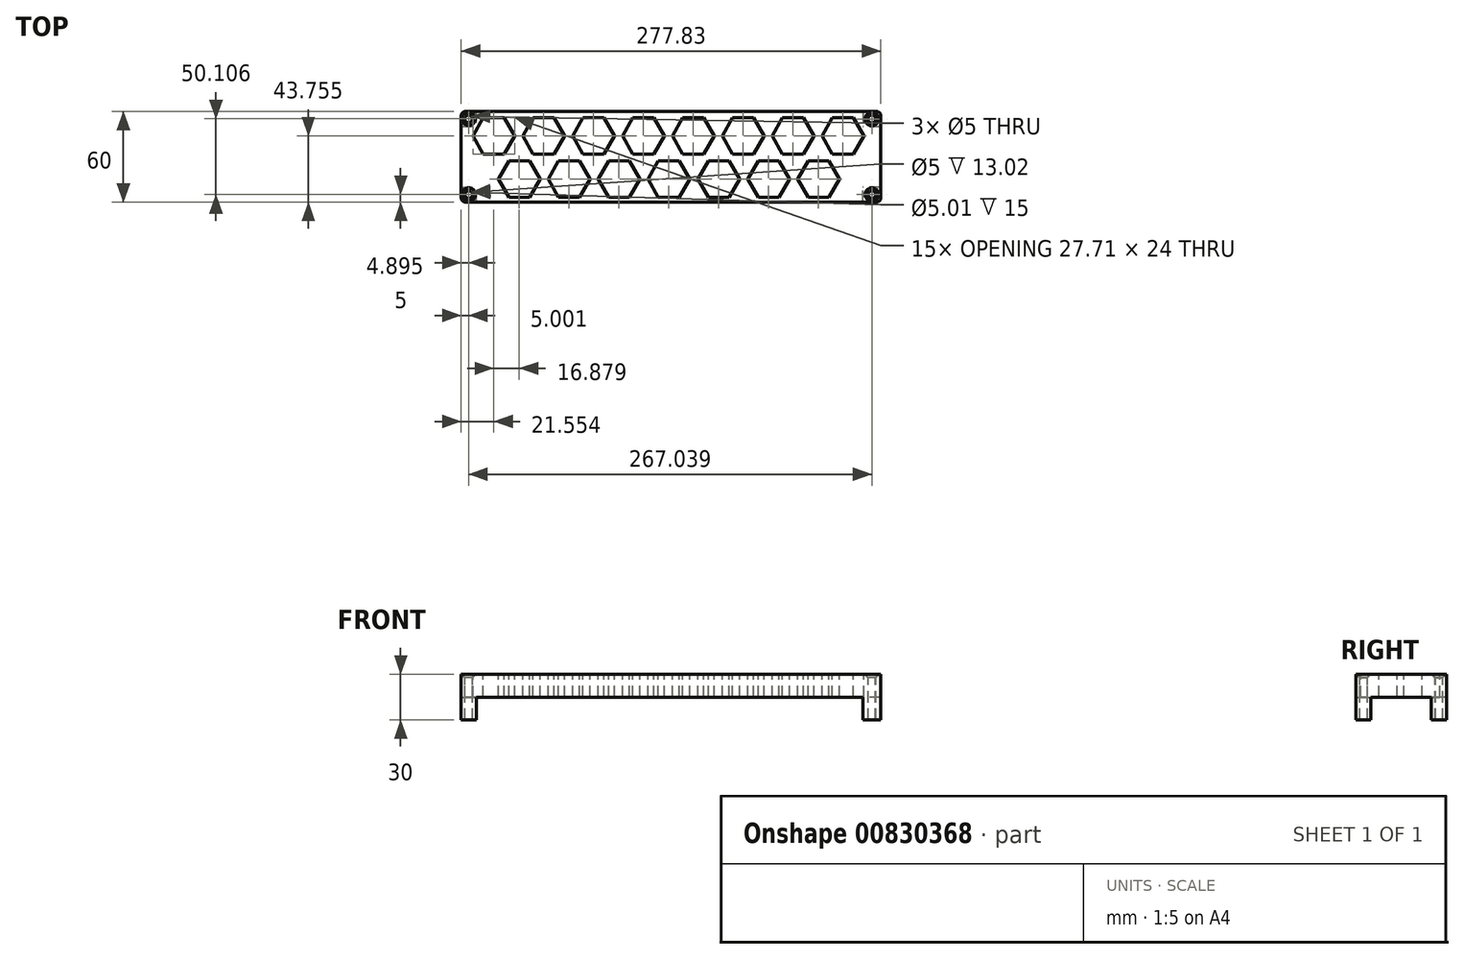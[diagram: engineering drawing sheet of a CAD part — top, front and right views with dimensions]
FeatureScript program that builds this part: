
annotation { "Feature Type Name" : "Feature", "Feature Type Description" : "" }
export const myFeature = defineFeature(function(context is Context, id is Id, definition is map)
    precondition{}
    {
        {
            var Q0;
            Q0=qCreatedBy(makeId("Top.planeOp"),FACE);
            var sketch = newSketch(context, id + "F0", { "sketchPlane" : qUnion([Q0])});
            skLineSegment(sketch, "E0.bottom", {"start": v(-54.94, 35.9) * mm, "end": v(215.06, 35.9) * mm});
            skLineSegment(sketch, "E0.top", {"start": v(-54.94, -24.1) * mm, "end": v(215.06, -24.1) * mm});
            skLineSegment(sketch, "E0.left", {"start": v(-54.94, 35.9) * mm, "end": v(-54.94, -24.1) * mm});
            skLineSegment(sketch, "E1.bottom", {"start": v(215.06, -24.1) * mm, "end": v(222.9, -24.1) * mm});
            skLineSegment(sketch, "E1.right", {"start": v(222.9, -24.1) * mm, "end": v(222.9, 35.9) * mm});
            skLineSegment(sketch, "E2", {"start": v(215.06, 35.9) * mm, "end": v(222.9, 35.9) * mm});
            skSolve(sketch);
        }
        {
            var Q0;
            Q0=makeQuery(id+"F0.imprint","IMPRINT",FACE,{"disambiguationData":[TD([[makeQuery(id+"F0.imprint","IMPRINT",EDGE,{"derivedFrom":sQuery(id+"F0.wireOp",EDGE,"E0.bottom")}),-1.0]])]});
            extrude(context, id + "F1", {"entities" : qUnion([Q0]), "depth" : 15 * mm, "offsetDistance" : 25.4 * mm});
        }
        {
            var Q0;
            Q0=makeQuery(id+"F1.opExtrude","CAP_FACE",FACE,{"disambiguationData":[OSD([sQuery(id+"F0.wireOp",EDGE,"E0.bottom"),sQuery(id+"F0.wireOp",EDGE,"E0.top"),sQuery(id+"F0.wireOp",EDGE,"E0.left"),sQuery(id+"F0.wireOp",EDGE,"E0.right")])],"isStart":false});
            var sketch = newSketch(context, id + "F2", { "sketchPlane" : qUnion([Q0])});
            skCircle(sketch, "E3.cCircle", {"center": v(-33.39, 19.66) * mm, "radius": 12 * mm, "construction": true});
            skLineSegment(sketch, "E3.0", {"start": v(-26.46, 7.66) * mm, "end": v(-40.31, 7.66) * mm});
            skLineSegment(sketch, "E3.1", {"start": v(-40.31, 7.66) * mm, "end": v(-47.24, 19.66) * mm});
            skLineSegment(sketch, "E3.2", {"start": v(-47.24, 19.66) * mm, "end": v(-40.31, 31.66) * mm});
            skLineSegment(sketch, "E3.3", {"start": v(-40.31, 31.66) * mm, "end": v(-26.46, 31.66) * mm});
            skLineSegment(sketch, "E3.4", {"start": v(-26.46, 31.66) * mm, "end": v(-19.53, 19.66) * mm});
            skLineSegment(sketch, "E3.5", {"start": v(-19.53, 19.66) * mm, "end": v(-26.46, 7.66) * mm});
            skPoint(sketch, "E3.0.midPoint", {"position": v(-33.39, 7.66) * mm});
            skLineSegment(sketch, "E4.1.0.0", {"start": v(6.56, 31.66) * mm, "end": v(13.5, 19.66) * mm});
            skLineSegment(sketch, "E4.1.0.1", {"start": v(-7.3, 31.66) * mm, "end": v(6.56, 31.66) * mm});
            skCircle(sketch, "E4.1.0.2", {"center": v(-0.37, 19.66) * mm, "radius": 12 * mm, "construction": true});
            skLineSegment(sketch, "E4.1.0.3", {"start": v(-14.22, 19.66) * mm, "end": v(-7.3, 31.66) * mm});
            skLineSegment(sketch, "E4.1.0.4", {"start": v(-7.3, 7.66) * mm, "end": v(-14.22, 19.66) * mm});
            skLineSegment(sketch, "E4.1.0.5", {"start": v(6.56, 7.66) * mm, "end": v(-7.3, 7.66) * mm});
            skLineSegment(sketch, "E4.1.0.6", {"start": v(13.5, 19.66) * mm, "end": v(6.56, 7.66) * mm});
            skLineSegment(sketch, "E4.2.0.0", {"start": v(39.58, 31.66) * mm, "end": v(46.51, 19.66) * mm});
            skLineSegment(sketch, "E4.2.0.1", {"start": v(25.73, 31.66) * mm, "end": v(39.58, 31.66) * mm});
            skCircle(sketch, "E4.2.0.2", {"center": v(32.65, 19.66) * mm, "radius": 12 * mm, "construction": true});
            skLineSegment(sketch, "E4.2.0.3", {"start": v(18.8, 19.66) * mm, "end": v(25.73, 31.66) * mm});
            skLineSegment(sketch, "E4.2.0.4", {"start": v(25.73, 7.66) * mm, "end": v(18.8, 19.66) * mm});
            skLineSegment(sketch, "E4.2.0.5", {"start": v(39.58, 7.66) * mm, "end": v(25.73, 7.66) * mm});
            skLineSegment(sketch, "E4.2.0.6", {"start": v(46.51, 19.66) * mm, "end": v(39.58, 7.66) * mm});
            skLineSegment(sketch, "E4.3.0.0", {"start": v(72.6, 31.66) * mm, "end": v(79.53, 19.66) * mm});
            skLineSegment(sketch, "E4.3.0.1", {"start": v(58.75, 31.66) * mm, "end": v(72.6, 31.66) * mm});
            skCircle(sketch, "E4.3.0.2", {"center": v(65.67, 19.66) * mm, "radius": 12 * mm, "construction": true});
            skLineSegment(sketch, "E4.3.0.3", {"start": v(51.82, 19.66) * mm, "end": v(58.75, 31.66) * mm});
            skLineSegment(sketch, "E4.3.0.4", {"start": v(58.75, 7.66) * mm, "end": v(51.82, 19.66) * mm});
            skLineSegment(sketch, "E4.3.0.5", {"start": v(72.6, 7.66) * mm, "end": v(58.75, 7.66) * mm});
            skLineSegment(sketch, "E4.3.0.6", {"start": v(79.53, 19.66) * mm, "end": v(72.6, 7.66) * mm});
            skLineSegment(sketch, "E4.4.0.0", {"start": v(105.62, 31.66) * mm, "end": v(112.55, 19.66) * mm});
            skLineSegment(sketch, "E4.4.0.1", {"start": v(91.77, 31.66) * mm, "end": v(105.62, 31.66) * mm});
            skCircle(sketch, "E4.4.0.2", {"center": v(98.7, 19.66) * mm, "radius": 12 * mm, "construction": true});
            skLineSegment(sketch, "E4.4.0.3", {"start": v(84.84, 19.66) * mm, "end": v(91.77, 31.66) * mm});
            skLineSegment(sketch, "E4.4.0.4", {"start": v(91.77, 7.66) * mm, "end": v(84.84, 19.66) * mm});
            skLineSegment(sketch, "E4.4.0.5", {"start": v(105.62, 7.66) * mm, "end": v(91.77, 7.66) * mm});
            skLineSegment(sketch, "E4.4.0.6", {"start": v(112.55, 19.66) * mm, "end": v(105.62, 7.66) * mm});
            skLineSegment(sketch, "E4.5.0.0", {"start": v(138.64, 31.66) * mm, "end": v(145.57, 19.66) * mm});
            skLineSegment(sketch, "E4.5.0.1", {"start": v(124.79, 31.66) * mm, "end": v(138.64, 31.66) * mm});
            skCircle(sketch, "E4.5.0.2", {"center": v(131.71, 19.66) * mm, "radius": 12 * mm, "construction": true});
            skLineSegment(sketch, "E4.5.0.3", {"start": v(117.86, 19.66) * mm, "end": v(124.79, 31.66) * mm});
            skLineSegment(sketch, "E4.5.0.4", {"start": v(124.79, 7.66) * mm, "end": v(117.86, 19.66) * mm});
            skLineSegment(sketch, "E4.5.0.5", {"start": v(138.64, 7.66) * mm, "end": v(124.79, 7.66) * mm});
            skLineSegment(sketch, "E4.5.0.6", {"start": v(145.57, 19.66) * mm, "end": v(138.64, 7.66) * mm});
            skLineSegment(sketch, "E4.6.0.0", {"start": v(171.66, 31.66) * mm, "end": v(178.6, 19.66) * mm});
            skLineSegment(sketch, "E4.6.0.1", {"start": v(157.8, 31.66) * mm, "end": v(171.66, 31.66) * mm});
            skCircle(sketch, "E4.6.0.2", {"center": v(164.73, 19.66) * mm, "radius": 12 * mm, "construction": true});
            skLineSegment(sketch, "E4.6.0.3", {"start": v(150.88, 19.66) * mm, "end": v(157.8, 31.66) * mm});
            skLineSegment(sketch, "E4.6.0.4", {"start": v(157.8, 7.66) * mm, "end": v(150.88, 19.66) * mm});
            skLineSegment(sketch, "E4.6.0.5", {"start": v(171.66, 7.66) * mm, "end": v(157.8, 7.66) * mm});
            skLineSegment(sketch, "E4.6.0.6", {"start": v(178.6, 19.66) * mm, "end": v(171.66, 7.66) * mm});
            skLineSegment(sketch, "E4.7.0.0", {"start": v(204.68, 31.66) * mm, "end": v(211.61, 19.66) * mm});
            skLineSegment(sketch, "E4.7.0.1", {"start": v(190.83, 31.66) * mm, "end": v(204.68, 31.66) * mm});
            skCircle(sketch, "E4.7.0.2", {"center": v(197.75, 19.66) * mm, "radius": 12 * mm, "construction": true});
            skLineSegment(sketch, "E4.7.0.3", {"start": v(183.9, 19.66) * mm, "end": v(190.83, 31.66) * mm});
            skLineSegment(sketch, "E4.7.0.4", {"start": v(190.83, 7.66) * mm, "end": v(183.9, 19.66) * mm});
            skLineSegment(sketch, "E4.7.0.5", {"start": v(204.68, 7.66) * mm, "end": v(190.83, 7.66) * mm});
            skLineSegment(sketch, "E4.7.0.6", {"start": v(211.61, 19.66) * mm, "end": v(204.68, 7.66) * mm});
            skLineSegment(sketch, "E4.direction1", {"start": v(-19.53, 19.66) * mm, "end": v(13.5, 19.66) * mm, "construction": true});
            skSolve(sketch);
        }
        {
            var Q0;
            Q0=makeQuery(id+"F2.imprint","IMPRINT",FACE,{"disambiguationData":[TD([[makeQuery(id+"F2.imprint","IMPRINT",EDGE,{"derivedFrom":sQuery(id+"F2.wireOp",EDGE,"E3.0")}),1.0]])]});
            var sketch = newSketch(context, id + "F3", { "sketchPlane" : qUnion([Q0])});
            skCircle(sketch, "E5.cCircle", {"center": v(-16.5, -8.82) * mm, "radius": 12 * mm, "construction": true});
            skLineSegment(sketch, "E5.0", {"start": v(-9.58, -20.82) * mm, "end": v(-23.44, -20.82) * mm});
            skLineSegment(sketch, "E5.1", {"start": v(-23.44, -20.82) * mm, "end": v(-30.36, -8.82) * mm});
            skLineSegment(sketch, "E5.2", {"start": v(-30.36, -8.82) * mm, "end": v(-23.44, 3.18) * mm});
            skLineSegment(sketch, "E5.3", {"start": v(-23.44, 3.18) * mm, "end": v(-9.58, 3.18) * mm});
            skLineSegment(sketch, "E5.4", {"start": v(-9.58, 3.18) * mm, "end": v(-2.65, -8.82) * mm});
            skLineSegment(sketch, "E5.5", {"start": v(-2.65, -8.82) * mm, "end": v(-9.58, -20.82) * mm});
            skPoint(sketch, "E5.0.midPoint", {"position": v(-16.5, -20.82) * mm});
            skLineSegment(sketch, "E6.1.0.0", {"start": v(9.58, 3.18) * mm, "end": v(23.44, 3.18) * mm});
            skLineSegment(sketch, "E6.1.0.1", {"start": v(23.44, 3.18) * mm, "end": v(30.37, -8.82) * mm});
            skLineSegment(sketch, "E6.1.0.2", {"start": v(2.66, -8.82) * mm, "end": v(9.58, 3.18) * mm});
            skLineSegment(sketch, "E6.1.0.3", {"start": v(9.58, -20.82) * mm, "end": v(2.66, -8.82) * mm});
            skLineSegment(sketch, "E6.1.0.4", {"start": v(23.44, -20.82) * mm, "end": v(9.58, -20.82) * mm});
            skLineSegment(sketch, "E6.1.0.5", {"start": v(30.37, -8.82) * mm, "end": v(23.44, -20.82) * mm});
            skLineSegment(sketch, "E6.2.0.0", {"start": v(42.6, 3.18) * mm, "end": v(56.46, 3.18) * mm});
            skLineSegment(sketch, "E6.2.0.1", {"start": v(56.46, 3.18) * mm, "end": v(63.39, -8.82) * mm});
            skLineSegment(sketch, "E6.2.0.2", {"start": v(35.68, -8.82) * mm, "end": v(42.6, 3.18) * mm});
            skLineSegment(sketch, "E6.2.0.3", {"start": v(42.6, -20.82) * mm, "end": v(35.68, -8.82) * mm});
            skLineSegment(sketch, "E6.2.0.4", {"start": v(56.46, -20.82) * mm, "end": v(42.6, -20.82) * mm});
            skLineSegment(sketch, "E6.2.0.5", {"start": v(63.39, -8.82) * mm, "end": v(56.46, -20.82) * mm});
            skLineSegment(sketch, "E6.3.0.0", {"start": v(75.62, 3.18) * mm, "end": v(89.48, 3.18) * mm});
            skLineSegment(sketch, "E6.3.0.1", {"start": v(89.48, 3.18) * mm, "end": v(96.4, -8.82) * mm});
            skLineSegment(sketch, "E6.3.0.2", {"start": v(68.7, -8.82) * mm, "end": v(75.62, 3.18) * mm});
            skLineSegment(sketch, "E6.3.0.3", {"start": v(75.62, -20.82) * mm, "end": v(68.7, -8.82) * mm});
            skLineSegment(sketch, "E6.3.0.4", {"start": v(89.48, -20.82) * mm, "end": v(75.62, -20.82) * mm});
            skLineSegment(sketch, "E6.3.0.5", {"start": v(96.4, -8.82) * mm, "end": v(89.48, -20.82) * mm});
            skLineSegment(sketch, "E6.4.0.0", {"start": v(108.64, 3.18) * mm, "end": v(122.5, 3.18) * mm});
            skLineSegment(sketch, "E6.4.0.1", {"start": v(122.5, 3.18) * mm, "end": v(129.43, -8.82) * mm});
            skLineSegment(sketch, "E6.4.0.2", {"start": v(101.72, -8.82) * mm, "end": v(108.64, 3.18) * mm});
            skLineSegment(sketch, "E6.4.0.3", {"start": v(108.64, -20.82) * mm, "end": v(101.72, -8.82) * mm});
            skLineSegment(sketch, "E6.4.0.4", {"start": v(122.5, -20.82) * mm, "end": v(108.64, -20.82) * mm});
            skLineSegment(sketch, "E6.4.0.5", {"start": v(129.43, -8.82) * mm, "end": v(122.5, -20.82) * mm});
            skLineSegment(sketch, "E6.5.0.0", {"start": v(141.66, 3.18) * mm, "end": v(155.52, 3.18) * mm});
            skLineSegment(sketch, "E6.5.0.1", {"start": v(155.52, 3.18) * mm, "end": v(162.45, -8.82) * mm});
            skLineSegment(sketch, "E6.5.0.2", {"start": v(134.74, -8.82) * mm, "end": v(141.66, 3.18) * mm});
            skLineSegment(sketch, "E6.5.0.3", {"start": v(141.66, -20.82) * mm, "end": v(134.74, -8.82) * mm});
            skLineSegment(sketch, "E6.5.0.4", {"start": v(155.52, -20.82) * mm, "end": v(141.66, -20.82) * mm});
            skLineSegment(sketch, "E6.5.0.5", {"start": v(162.45, -8.82) * mm, "end": v(155.52, -20.82) * mm});
            skLineSegment(sketch, "E6.6.0.0", {"start": v(174.68, 3.18) * mm, "end": v(188.54, 3.18) * mm});
            skLineSegment(sketch, "E6.6.0.1", {"start": v(188.54, 3.18) * mm, "end": v(195.47, -8.82) * mm});
            skLineSegment(sketch, "E6.6.0.2", {"start": v(167.76, -8.82) * mm, "end": v(174.68, 3.18) * mm});
            skLineSegment(sketch, "E6.6.0.3", {"start": v(174.68, -20.82) * mm, "end": v(167.76, -8.82) * mm});
            skLineSegment(sketch, "E6.6.0.4", {"start": v(188.54, -20.82) * mm, "end": v(174.68, -20.82) * mm});
            skLineSegment(sketch, "E6.6.0.5", {"start": v(195.47, -8.82) * mm, "end": v(188.54, -20.82) * mm});
            skLineSegment(sketch, "E6.direction1", {"start": v(-23.44, 3.18) * mm, "end": v(9.58, 3.18) * mm, "construction": true});
            skSolve(sketch);
        }
        {
            var Q0;
            Q0=makeQuery(id+"F2.imprint","IMPRINT",FACE,{"disambiguationData":[TD([[makeQuery(id+"F2.imprint","IMPRINT",EDGE,{"derivedFrom":sQuery(id+"F2.wireOp",EDGE,"E3.0")}),-1.0]])]});
            var Q1;
            Q1=makeQuery(id+"F3.imprint","IMPRINT",FACE,{"disambiguationData":[TD([[makeQuery(id+"F3.imprint","IMPRINT",EDGE,{"derivedFrom":sQuery(id+"F3.wireOp",EDGE,"E5.0")}),-1.0]])]});
            var Q2;
            Q2=makeQuery(id+"F2.imprint","IMPRINT",FACE,{"disambiguationData":[TD([[makeQuery(id+"F2.imprint","IMPRINT",EDGE,{"derivedFrom":sQuery(id+"F2.wireOp",EDGE,"E4.1.0.0")}),-1.0]])]});
            var Q3;
            Q3=makeQuery(id+"F2.imprint","IMPRINT",FACE,{"disambiguationData":[TD([[makeQuery(id+"F2.imprint","IMPRINT",EDGE,{"derivedFrom":sQuery(id+"F2.wireOp",EDGE,"E4.2.0.0")}),-1.0]])]});
            var Q4;
            Q4=makeQuery(id+"F2.imprint","IMPRINT",FACE,{"disambiguationData":[TD([[makeQuery(id+"F2.imprint","IMPRINT",EDGE,{"derivedFrom":sQuery(id+"F2.wireOp",EDGE,"E4.3.0.0")}),-1.0]])]});
            var Q5;
            Q5=makeQuery(id+"F2.imprint","IMPRINT",FACE,{"disambiguationData":[TD([[makeQuery(id+"F2.imprint","IMPRINT",EDGE,{"derivedFrom":sQuery(id+"F2.wireOp",EDGE,"E4.4.0.0")}),-1.0]])]});
            var Q6;
            Q6=makeQuery(id+"F2.imprint","IMPRINT",FACE,{"disambiguationData":[TD([[makeQuery(id+"F2.imprint","IMPRINT",EDGE,{"derivedFrom":sQuery(id+"F2.wireOp",EDGE,"E4.5.0.0")}),-1.0]])]});
            var Q7;
            Q7=makeQuery(id+"F2.imprint","IMPRINT",FACE,{"disambiguationData":[TD([[makeQuery(id+"F2.imprint","IMPRINT",EDGE,{"derivedFrom":sQuery(id+"F2.wireOp",EDGE,"E4.6.0.0")}),-1.0]])]});
            var Q8;
            Q8=makeQuery(id+"F2.imprint","IMPRINT",FACE,{"disambiguationData":[TD([[makeQuery(id+"F2.imprint","IMPRINT",EDGE,{"derivedFrom":sQuery(id+"F2.wireOp",EDGE,"E4.7.0.0")}),-1.0]])]});
            var Q9;
            Q9=makeQuery(id+"F3.imprint","IMPRINT",FACE,{"disambiguationData":[TD([[makeQuery(id+"F3.imprint","IMPRINT",EDGE,{"derivedFrom":sQuery(id+"F3.wireOp",EDGE,"E6.1.0.0")}),-1.0]])]});
            extrude(context, id + "F4", {"entities" : qUnion([Q0, Q1, Q2, Q3, Q4, Q5, Q6, Q7, Q8, Q9]), "operationType" : NewBodyOperationType.REMOVE, "oppositeDirection" : true, "depth" : 61.47 * mm, "offsetDistance" : 25.4 * mm});
        }
        {
            var Q0;
            Q0=makeQuery(id+"F3.imprint","IMPRINT",FACE,{"disambiguationData":[TD([[makeQuery(id+"F3.imprint","IMPRINT",EDGE,{"derivedFrom":sQuery(id+"F3.wireOp",EDGE,"E6.2.0.0")}),-1.0]])]});
            var Q1;
            Q1=makeQuery(id+"F3.imprint","IMPRINT",FACE,{"disambiguationData":[TD([[makeQuery(id+"F3.imprint","IMPRINT",EDGE,{"derivedFrom":sQuery(id+"F3.wireOp",EDGE,"E6.3.0.0")}),-1.0]])]});
            var Q2;
            Q2=makeQuery(id+"F3.imprint","IMPRINT",FACE,{"disambiguationData":[TD([[makeQuery(id+"F3.imprint","IMPRINT",EDGE,{"derivedFrom":sQuery(id+"F3.wireOp",EDGE,"E6.4.0.0")}),-1.0]])]});
            var Q3;
            Q3=makeQuery(id+"F3.imprint","IMPRINT",FACE,{"disambiguationData":[TD([[makeQuery(id+"F3.imprint","IMPRINT",EDGE,{"derivedFrom":sQuery(id+"F3.wireOp",EDGE,"E6.5.0.0")}),-1.0]])]});
            var Q4;
            Q4=makeQuery(id+"F3.imprint","IMPRINT",FACE,{"disambiguationData":[TD([[makeQuery(id+"F3.imprint","IMPRINT",EDGE,{"derivedFrom":sQuery(id+"F3.wireOp",EDGE,"E6.6.0.0")}),-1.0]])]});
            extrude(context, id + "F5", {"entities" : qUnion([Q0, Q1, Q2, Q3, Q4]), "operationType" : NewBodyOperationType.REMOVE, "oppositeDirection" : true, "depth" : 25.4 * mm, "offsetDistance" : 25.4 * mm});
        }
        {
            var Q0;
            Q0=makeQuery(id+"F3.imprint","IMPRINT",FACE,{"disambiguationData":[TD([[makeQuery(id+"F3.imprint","IMPRINT",EDGE,{"derivedFrom":sQuery(id+"F3.wireOp",EDGE,"E5.0")}),1.0]])]});
            var sketch = newSketch(context, id + "F6", { "sketchPlane" : qUnion([Q0])});
            skLineSegment(sketch, "E7.0", {"start": v(-49.94, 30.9) * mm, "end": v(217, 30.9) * mm});
            skLineSegment(sketch, "E7.1", {"start": v(-49.94, 30.9) * mm, "end": v(-49.94, -19.1) * mm});
            skLineSegment(sketch, "E7.2", {"start": v(-49.94, -19.1) * mm, "end": v(217, -19.1) * mm});
            skLineSegment(sketch, "E7.3", {"start": v(217, 30.9) * mm, "end": v(217, -19.1) * mm});
            skSolve(sketch);
        }
        {
            var Q0;
            Q0=makeQuery(id+"F3.imprint","IMPRINT",FACE,{"disambiguationData":[TD([[makeQuery(id+"F3.imprint","IMPRINT",EDGE,{"derivedFrom":sQuery(id+"F3.wireOp",EDGE,"E5.0")}),1.0]])]});
            var sketch = newSketch(context, id + "F7", { "sketchPlane" : qUnion([Q0])});
            skCircle(sketch, "E8", {"center": v(-50.04, 31.02) * mm, "radius": 1.21 * mm});
            skCircle(sketch, "E9", {"center": v(-49.99, -19.03) * mm, "radius": 1.66 * mm});
            skCircle(sketch, "E10", {"center": v(216.9, 30.9) * mm, "radius": 1.94 * mm});
            skCircle(sketch, "E11", {"center": v(216.97, -19.22) * mm, "radius": 2.58 * mm});
            skSolve(sketch);
        }
        {
            var Q0;
            Q0=sQuery(id+"F6.wireOp",VERTEX,"E7.2.end");
            var Q1;
            Q1=sQuery(id+"F7.wireOp",VERTEX,"E10.center");
            var Q2;
            Q2=sQuery(id+"F6.wireOp",VERTEX,"E7.1.end");
            var Q3;
            Q3=sQuery(id+"F7.wireOp",VERTEX,"E8.center");
            var Q4;
            Q4=makeQuery(id+"F1.opExtrude","SWEPT_BODY",BODY,{"disambiguationData":[OSD([sQuery(id+"F0.wireOp",EDGE,"E0.bottom"),sQuery(id+"F0.wireOp",EDGE,"E0.top"),sQuery(id+"F0.wireOp",EDGE,"E0.left"),sQuery(id+"F0.wireOp",EDGE,"E1.bottom"),sQuery(id+"F0.wireOp",EDGE,"E1.right"),sQuery(id+"F0.wireOp",EDGE,"E2")])]});
            hole(context, id + "F8", {"style" : HoleStyle.C_SINK, "endStyle" : HoleEndStyle.THROUGH, "standardTappedOrClearance" : lookupTablePath({ "standard" : "ISO", "size" : "5", "type" : "Drilled" }), "standardBlindInLast" : lookupTablePath({ "standard" : "ISO", "size" : "5", "type" : "Drilled" }), "holeDiameter" : 5 * mm, "cSinkDiameter" : 8.96 * mm, "cSinkAngle" : 90 * degree, "majorDiameter" : 6.35 * mm, "isTappedThrough" : true, "tappedDepth" : 12.7 * mm, "tapClearance" : 3, "locations" : qUnion([Q0, Q1, Q2, Q3]), "scope" : qUnion([Q4])});
        }
        {
            var Q0;
            Q0=makeQuery(id+"F1.opExtrude","CAP_FACE",FACE,{"disambiguationData":[OSD([sQuery(id+"F0.wireOp",EDGE,"E0.bottom"),sQuery(id+"F0.wireOp",EDGE,"E0.top"),sQuery(id+"F0.wireOp",EDGE,"E0.left"),sQuery(id+"F0.wireOp",EDGE,"E1.bottom"),sQuery(id+"F0.wireOp",EDGE,"E1.right"),sQuery(id+"F0.wireOp",EDGE,"E2")])],"isStart":true});
            var sketch = newSketch(context, id + "F9", { "sketchPlane" : qUnion([Q0])});
            skLineSegment(sketch, "E12.bottom", {"start": v(-54.94, 24.1) * mm, "end": v(-44.94, 24.1) * mm});
            skLineSegment(sketch, "E12.top", {"start": v(-54.94, 14.1) * mm, "end": v(-44.94, 14.1) * mm});
            skLineSegment(sketch, "E12.left", {"start": v(-54.94, 24.1) * mm, "end": v(-54.94, 14.1) * mm});
            skLineSegment(sketch, "E12.right", {"start": v(-44.94, 24.1) * mm, "end": v(-44.94, 14.1) * mm});
            skPoint(sketch, "E12.middle", {"position": v(-49.94, 19.1) * mm});
            skLineSegment(sketch, "E13.bottom", {"start": v(-54.94, -35.9) * mm, "end": v(-45.15, -35.9) * mm});
            skLineSegment(sketch, "E13.top", {"start": v(-54.94, -26.12) * mm, "end": v(-45.15, -26.12) * mm});
            skLineSegment(sketch, "E13.left", {"start": v(-54.94, -35.9) * mm, "end": v(-54.94, -26.12) * mm});
            skLineSegment(sketch, "E13.right", {"start": v(-45.15, -35.9) * mm, "end": v(-45.15, -26.12) * mm});
            skPoint(sketch, "E13.middle", {"position": v(-50.04, -31.02) * mm});
            skLineSegment(sketch, "E14.bottom", {"start": v(222.9, 24.1) * mm, "end": v(211.1, 24.1) * mm});
            skLineSegment(sketch, "E14.top", {"start": v(222.9, 14.1) * mm, "end": v(211.1, 14.1) * mm});
            skLineSegment(sketch, "E14.left", {"start": v(222.9, 24.1) * mm, "end": v(222.9, 14.1) * mm});
            skLineSegment(sketch, "E14.right", {"start": v(211.1, 24.1) * mm, "end": v(211.1, 14.1) * mm});
            skPoint(sketch, "E14.middle", {"position": v(217, 19.1) * mm});
            skLineSegment(sketch, "E15.bottom", {"start": v(222.9, -35.9) * mm, "end": v(210.92, -35.9) * mm});
            skLineSegment(sketch, "E15.top", {"start": v(222.9, -25.9) * mm, "end": v(210.92, -25.9) * mm});
            skLineSegment(sketch, "E15.left", {"start": v(222.9, -35.9) * mm, "end": v(222.9, -25.9) * mm});
            skLineSegment(sketch, "E15.right", {"start": v(210.92, -35.9) * mm, "end": v(210.92, -25.9) * mm});
            skPoint(sketch, "E15.middle", {"position": v(216.9, -30.9) * mm});
            skCircle(sketch, "E16", {"center": v(216.9, -30.9) * mm, "radius": 2.44 * mm});
            skCircle(sketch, "E17", {"center": v(217, 19.1) * mm, "radius": 2.49 * mm});
            skCircle(sketch, "E18", {"center": v(-49.94, 19.1) * mm, "radius": 2.5 * mm});
            skCircle(sketch, "E19", {"center": v(-50.04, -31.02) * mm, "radius": 2.5 * mm});
            skSolve(sketch);
        }
        {
            var Q0;
            Q0=makeQuery(id+"F9.imprint","IMPRINT",FACE,{"disambiguationData":[TD([[makeQuery(id+"F9.imprint","IMPRINT",EDGE,{"derivedFrom":sQuery(id+"F9.wireOp",EDGE,"E13.bottom")}),1.0]])]});
            var Q1;
            Q1=makeQuery(id+"F9.imprint","IMPRINT",FACE,{"disambiguationData":[TD([[makeQuery(id+"F9.imprint","IMPRINT",EDGE,{"derivedFrom":sQuery(id+"F9.wireOp",EDGE,"E12.bottom")}),-1.0]])]});
            var Q2;
            Q2=makeQuery(id+"F9.imprint","IMPRINT",FACE,{"disambiguationData":[TD([[makeQuery(id+"F9.imprint","IMPRINT",EDGE,{"derivedFrom":sQuery(id+"F9.wireOp",EDGE,"E14.bottom")}),-1.0]])]});
            var Q3;
            Q3=makeQuery(id+"F9.imprint","IMPRINT",FACE,{"disambiguationData":[TD([[makeQuery(id+"F9.imprint","IMPRINT",EDGE,{"derivedFrom":sQuery(id+"F9.wireOp",EDGE,"E15.bottom")}),1.0]])]});
            extrude(context, id + "F10", {"entities" : qUnion([Q0, Q1, Q2, Q3]), "operationType" : NewBodyOperationType.ADD, "depth" : 15 * mm, "offsetDistance" : 25.4 * mm});
        }
        {
            var Q0;
            Q0=makeQuery(id+"F10.boolean.opBoolean","MERGE",EDGE,{"derivedFrom":[makeQuery(id+"F1.opExtrude","SWEPT_EDGE",EDGE,{"disambiguationData":[OSD([sQuery(id+"F0.wireOp",EDGE,"E0.top"),sQuery(id+"F0.wireOp",EDGE,"E0.left")])]}),makeQuery(id+"F10.opExtrude","SWEPT_EDGE",EDGE,{"disambiguationData":[OSD([sQuery(id+"F9.wireOp",EDGE,"E12.bottom"),sQuery(id+"F9.wireOp",EDGE,"E12.left")])]})]});
            var Q1;
            Q1=makeQuery(id+"F10.boolean.opBoolean","MERGE",EDGE,{"derivedFrom":[makeQuery(id+"F1.opExtrude","SWEPT_EDGE",EDGE,{"disambiguationData":[OSD([sQuery(id+"F0.wireOp",EDGE,"E0.bottom"),sQuery(id+"F0.wireOp",EDGE,"E0.left")])]}),makeQuery(id+"F10.opExtrude","SWEPT_EDGE",EDGE,{"disambiguationData":[OSD([sQuery(id+"F9.wireOp",EDGE,"E13.bottom"),sQuery(id+"F9.wireOp",EDGE,"E13.left")])]})]});
            var Q2;
            Q2=makeQuery(id+"F10.boolean.opBoolean","MERGE",EDGE,{"derivedFrom":[makeQuery(id+"F1.opExtrude","SWEPT_EDGE",EDGE,{"disambiguationData":[OSD([sQuery(id+"F0.wireOp",EDGE,"E1.bottom"),sQuery(id+"F0.wireOp",EDGE,"E1.right")])]}),makeQuery(id+"F10.opExtrude","SWEPT_EDGE",EDGE,{"disambiguationData":[OSD([sQuery(id+"F9.wireOp",EDGE,"E14.bottom"),sQuery(id+"F9.wireOp",EDGE,"E14.left")])]})]});
            var Q3;
            Q3=makeQuery(id+"F10.boolean.opBoolean","MERGE",EDGE,{"derivedFrom":[makeQuery(id+"F1.opExtrude","SWEPT_EDGE",EDGE,{"disambiguationData":[OSD([sQuery(id+"F0.wireOp",EDGE,"E1.right"),sQuery(id+"F0.wireOp",EDGE,"E2")])]}),makeQuery(id+"F10.opExtrude","SWEPT_EDGE",EDGE,{"disambiguationData":[OSD([sQuery(id+"F9.wireOp",EDGE,"E15.bottom"),sQuery(id+"F9.wireOp",EDGE,"E15.left")])]})]});
            fillet(context, id + "F11", {"entities" : qUnion([Q0, Q1, Q2, Q3]), "radius" : 3 * mm, "tangentPropagation" : true, "allowEdgeOverflow" : false});
        }
    });
